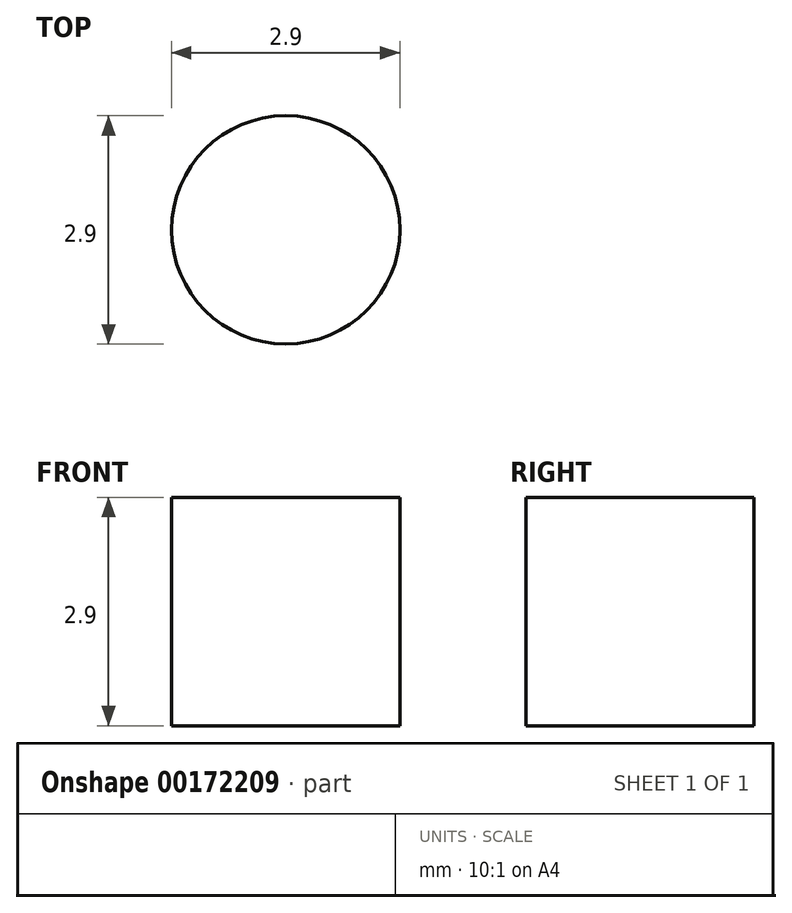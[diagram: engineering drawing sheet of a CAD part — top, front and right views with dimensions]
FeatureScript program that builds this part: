
annotation { "Feature Type Name" : "Feature", "Feature Type Description" : "" }
export const myFeature = defineFeature(function(context is Context, id is Id, definition is map)
    precondition{}
    {
        {
            var Q0;
            Q0=qCreatedBy(makeId("Top.planeOp"),FACE);
            var sketch = newSketch(context, id + "F0", { "sketchPlane" : qUnion([Q0])});
            skCircle(sketch, "E0", {"center": v(0, 0) * mm, "radius": 1.45 * mm});
            skSolve(sketch);
        }
        {
            var Q0;
            Q0=makeQuery(id+"F0.imprint","IMPRINT",FACE,{"disambiguationData":[TD([[makeQuery(id+"F0.imprint","IMPRINT",EDGE,{"derivedFrom":sQuery(id+"F0.wireOp",EDGE,"E0")}),1.0]])]});
            extrude(context, id + "F1", {"entities" : qUnion([Q0]), "depth" : 2.9 * mm});
        }
    });
